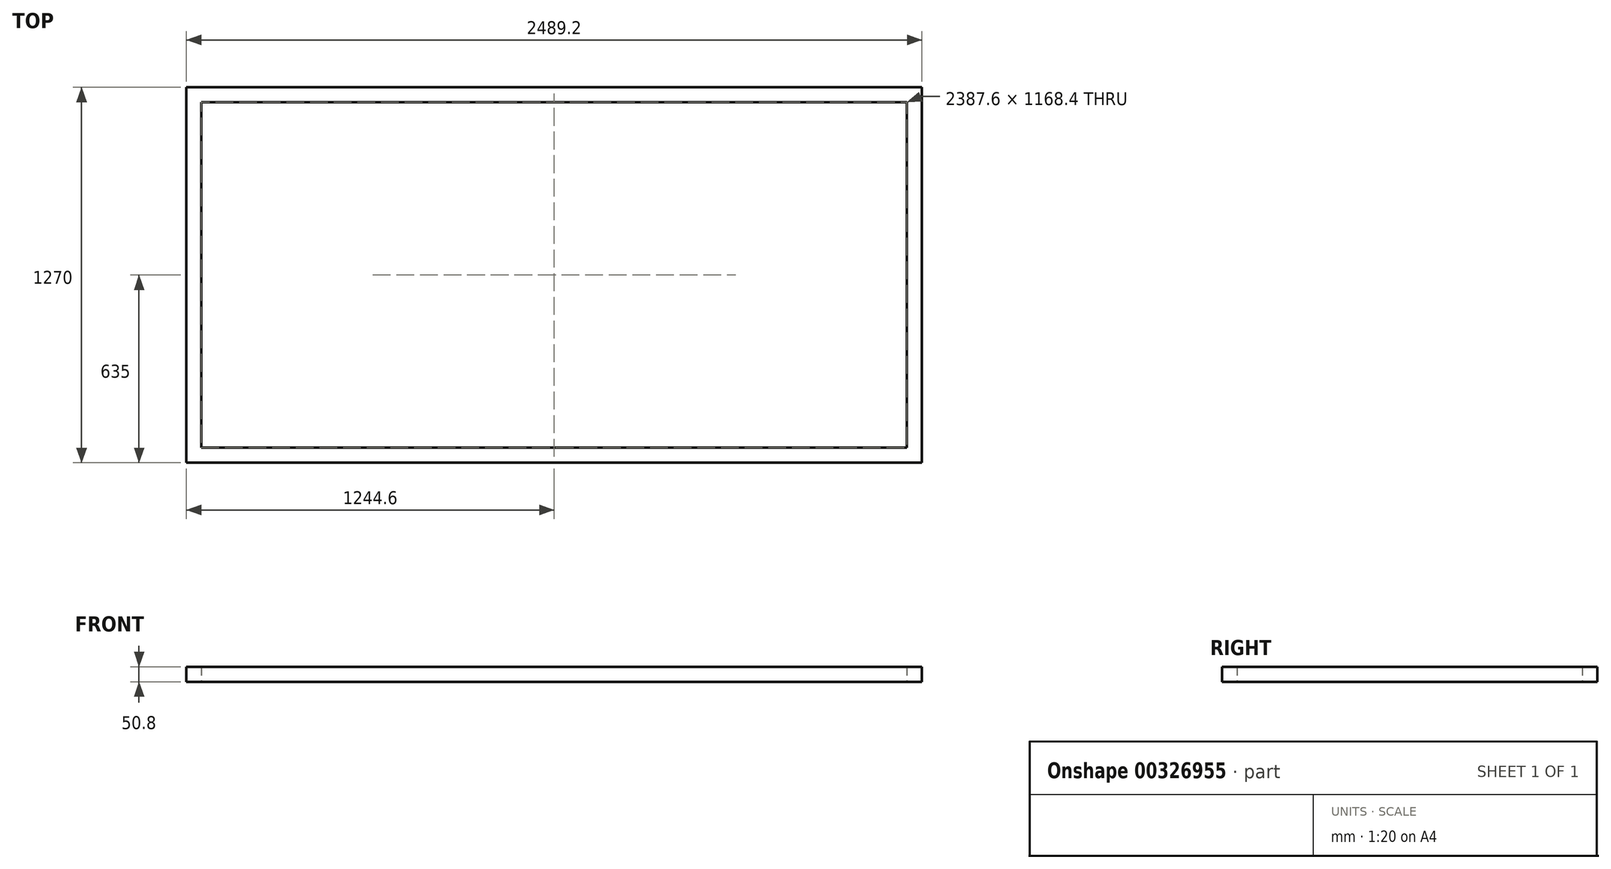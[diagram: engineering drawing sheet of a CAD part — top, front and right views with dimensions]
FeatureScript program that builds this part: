
annotation { "Feature Type Name" : "Feature", "Feature Type Description" : "" }
export const myFeature = defineFeature(function(context is Context, id is Id, definition is map)
    precondition{}
    {
        {
            var Q0;
            Q0=qCreatedBy(makeId("Top.planeOp"),FACE);
            var sketch = newSketch(context, id + "F0", { "sketchPlane" : qUnion([Q0])});
            skLineSegment(sketch, "E0", {"start": v(-1219.2, -609.6) * mm, "end": v(1219.2, -609.6) * mm});
            skLineSegment(sketch, "E1", {"start": v(1219.2, -609.6) * mm, "end": v(1219.2, 609.6) * mm});
            skLineSegment(sketch, "E2", {"start": v(1219.2, 609.6) * mm, "end": v(-1219.2, 609.6) * mm});
            skLineSegment(sketch, "E3", {"start": v(-1219.2, 609.6) * mm, "end": v(-1219.2, -609.6) * mm});
            skSolve(sketch);
        }
        {
            var Q0;
            Q0=qCreatedBy(makeId("Front.planeOp"),FACE);
            var sketch = newSketch(context, id + "F1", { "sketchPlane" : qUnion([Q0])});
            skLineSegment(sketch, "E4.bottom", {"start": v(-1244.6, -25.4) * mm, "end": v(-1193.8, -25.4) * mm});
            skLineSegment(sketch, "E4.top", {"start": v(-1244.6, 25.4) * mm, "end": v(-1193.8, 25.4) * mm});
            skLineSegment(sketch, "E4.left", {"start": v(-1244.6, -25.4) * mm, "end": v(-1244.6, 25.4) * mm});
            skLineSegment(sketch, "E4.right", {"start": v(-1193.8, -25.4) * mm, "end": v(-1193.8, 25.4) * mm});
            skLineSegment(sketch, "E5", {"start": v(-1244.6, 25.4) * mm, "end": v(-1193.8, -25.4) * mm, "construction": true});
            skSolve(sketch);
        }
        {
            var Q0;
            Q0=makeQuery(id+"F1.imprint","IMPRINT",FACE,{"disambiguationData":[TD([[makeQuery(id+"F1.imprint","IMPRINT",EDGE,{"derivedFrom":sQuery(id+"F1.wireOp",EDGE,"E4.bottom")}),1.0]])]});
            var Q1;
            Q1=sQuery(id+"F0.wireOp",EDGE,"E3");
            var Q2;
            Q2=sQuery(id+"F0.wireOp",EDGE,"E0");
            var Q3;
            Q3=sQuery(id+"F0.wireOp",EDGE,"E2");
            var Q4;
            Q4=sQuery(id+"F0.wireOp",EDGE,"E1");
            sweep(context, id + "F2", {"profiles" : qUnion([Q0]), "path" : qUnion([Q1, Q2, Q3, Q4])});
        }
    });
